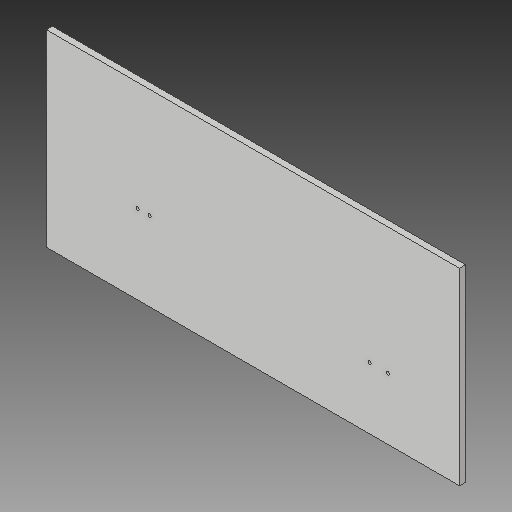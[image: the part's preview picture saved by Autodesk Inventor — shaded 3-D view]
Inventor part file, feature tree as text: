
AUTODESK INVENTOR PART (.ipt)
format: ipt  version: 2019 (Build 230136000, 136)  size: 123,392 bytes
history: native  units: in
note: dims shown in document units (in); Inventor stores cm internally (conversion verified against a paired STEP export)
features: sketch x3, hole x2, extrude x1, thicken_offset x1
ambient origin geometry x8: Origin, YZ Plane, XZ Plane, XY Plane, X Axis, Y Axis, Z Axis, Center Point
bodies: Solid1 (feature_tree)
feature tree (7):
  extrude  "Extrusion1"  Depth=6.0in
  thicken_offset  "Thicken1"
  hole  "Hole1"  [1 undecoded]
  hole  "Hole2"  [1 undecoded]
  sketch  "Sketch1"  dims[d0=17.0in d1=6.0in]
  sketch  "Sketch3"  dims[d2=0.25in d3=0.0in d4=1.75in]
  sketch  "Sketch5"  dims[d5=1.75in d8=3.06in d9=90.0deg d10=3.5in d11=1.0in d12=0.375in d13=0.25in d14=0.25in d15=0.13in d16=0.75in d17=0.375in d18=0.25in d19=0.5635in d20=1.0in d21=0.8108in d22=2.45in d23=0.0in d24=2.35in d25=90.0deg d26=0.0in d27=1.75in d28=0.375in d29=0.5in d30=0.5in d31=0.13in d32=0.75in d33=0.375in d34=0.25in d35=0.5635in d36=1.0in d37=0.8108in]
note: 2 required parameter values undecoded (feature->parameter linkage not recoverable at this tier; creation-order binding heuristic only, values carry confidence <= 0.55)
